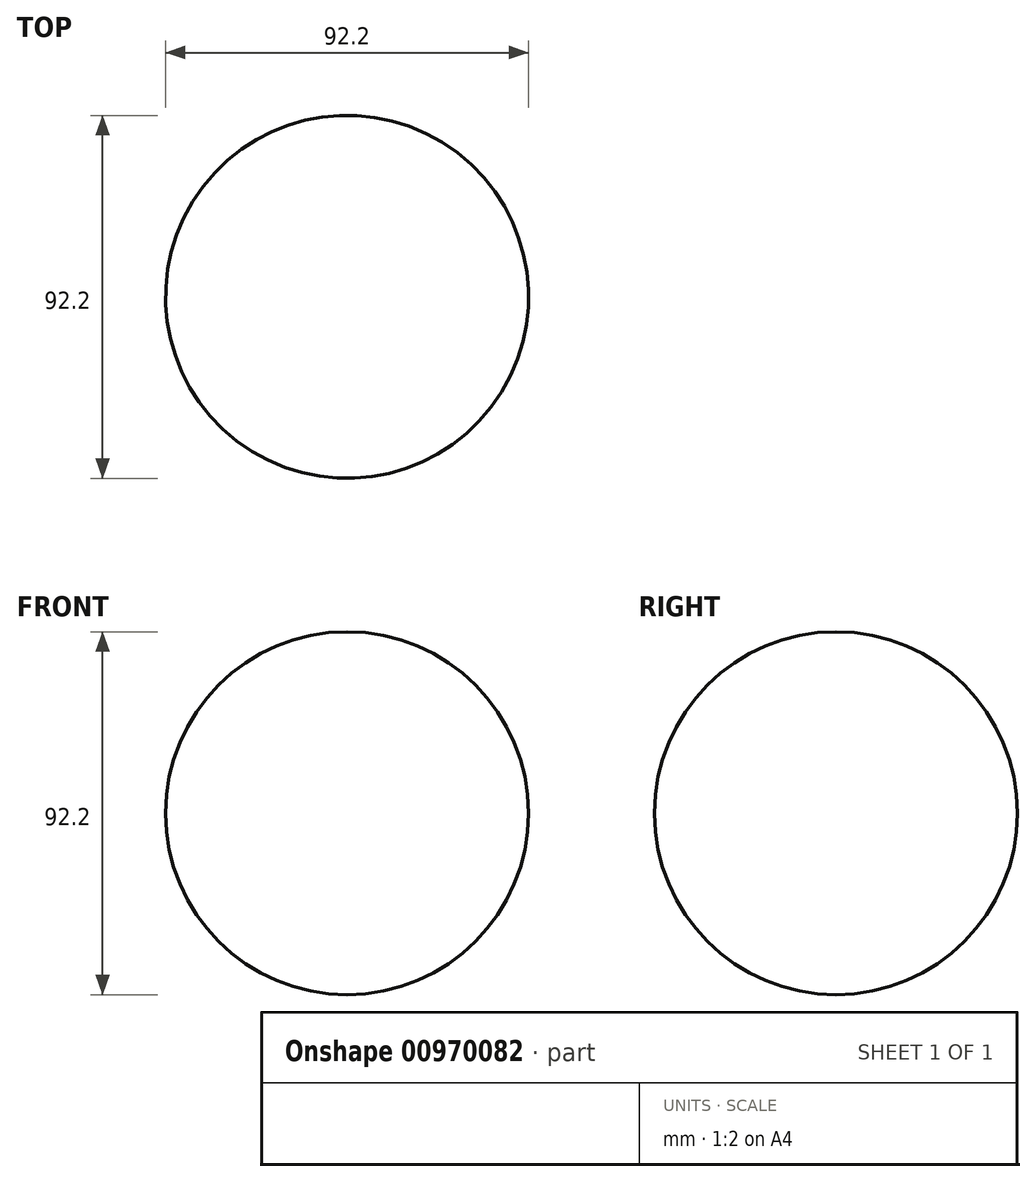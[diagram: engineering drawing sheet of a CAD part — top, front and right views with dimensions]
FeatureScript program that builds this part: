
annotation { "Feature Type Name" : "Feature", "Feature Type Description" : "" }
export const myFeature = defineFeature(function(context is Context, id is Id, definition is map)
    precondition{}
    {
        {
            var Q0;
            Q0=qCreatedBy(makeId("Top.planeOp"),FACE);
            var sketch = newSketch(context, id + "F0", { "sketchPlane" : qUnion([Q0])});
            skArc(sketch, "E0", {"start": v(-24.17, -39.25) * mm, "mid": v(39.25, -24.17) * mm, "end": v(24.17, 39.25) * mm});
            skLineSegment(sketch, "E1", {"start": v(0, 0) * mm, "end": v(24.17, 39.25) * mm});
            skLineSegment(sketch, "E2", {"start": v(24.17, 39.25) * mm, "end": v(0, 0) * mm});
            skLineSegment(sketch, "E3", {"start": v(0, 0) * mm, "end": v(-24.17, -39.25) * mm});
            skSolve(sketch);
        }
        {
            var Q0;
            Q0=makeQuery(id+"F0.imprint","IMPRINT",FACE,{"disambiguationData":[TD([[makeQuery(id+"F0.imprint","IMPRINT",EDGE,{"derivedFrom":sQuery(id+"F0.wireOp",EDGE,"E0")}),1.0]])]});
            var Q1;
            Q1=sQuery(id+"F0.wireOp",EDGE,"E1");
            revolve(context, id + "F1", {"surfaceOperationType" : NewSurfaceOperationType.NEW, "entities" : qUnion([Q0]), "axis" : qUnion([Q1]), "revolveType" : RevolveType.FULL});
        }
    });
